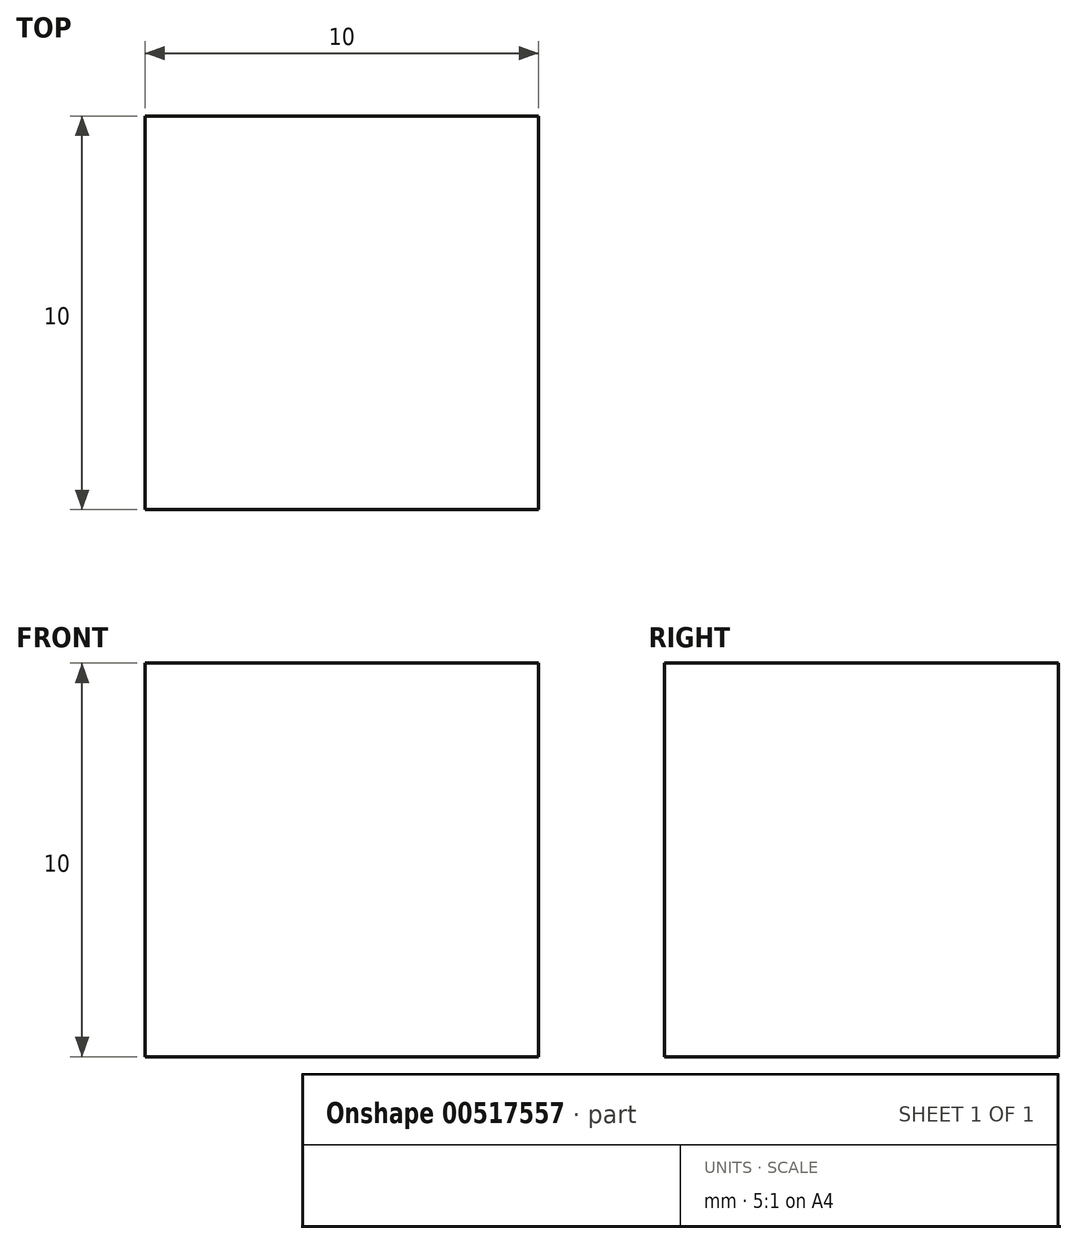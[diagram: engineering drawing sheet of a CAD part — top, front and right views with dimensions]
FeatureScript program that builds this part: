
annotation { "Feature Type Name" : "Feature", "Feature Type Description" : "" }
export const myFeature = defineFeature(function(context is Context, id is Id, definition is map)
    precondition{}
    {
        {
            var Q0;
            Q0=qCreatedBy(makeId("Top.planeOp"),FACE);
            var sketch = newSketch(context, id + "F0", { "sketchPlane" : qUnion([Q0])});
            skLineSegment(sketch, "E0.bottom", {"start": v(-5, 5) * mm, "end": v(5, 5) * mm});
            skLineSegment(sketch, "E0.top", {"start": v(-5, -5) * mm, "end": v(5, -5) * mm});
            skLineSegment(sketch, "E0.left", {"start": v(-5, 5) * mm, "end": v(-5, -5) * mm});
            skLineSegment(sketch, "E0.right", {"start": v(5, 5) * mm, "end": v(5, -5) * mm});
            skPoint(sketch, "E0.middle", {"position": v(0, 0) * mm});
            skSolve(sketch);
        }
        {
            var Q0;
            Q0 = qSketchRegion(id + "F0", true);
            extrude(context, id + "F1", {"entities" : qUnion([Q0]), "depth" : 10 * mm, "offsetDistance" : 25 * mm});
        }
    });
